# Revit family: Sink-Wall_Hung-American Standard-Comrade-0124.024
name_source: partatom
category: Plumbing Fixtures
units: mm (PartAtom-declared; Revit-internal decimal feet)

## family parameters
Cut with Voids When Loaded = No
Host = Face
OmniClass Number = 23.45.05.14.14
OmniClass Title = Sinks/Lavatories
Part Type = Normal
Room Calculation Point = No
Round Connector Dimension = Use Diameter
Shared = Yes

## types (1)
- 0124024.020
    ASME A112.19.2M for Vitreous China Fixtures = Yes
    Assembly Code = D2010310
    Bowl Depth = 6 1/4"
    CW Connection = Yes
    CWFU = 1.5
    Cold Water Connection Diameter = 1/2"
    Default Elevation = 30"
    Description = Comrade™ Wall-Hung Sink With 4-Inch Centerset, Wall Hanger Included
    Elevation Adjustment = 31"
    Finish = Vitreous China-American Standard-020-White
    HW Connection = Yes
    HWFU = 1.5
    Height = 9 1/2"
    Hot Water Connection Diameter = 1/2"
    Length = 18 1/4"
    Manufacturer = American Standard
    Material = Vitreous China-American Standard-020-White
    Model = 0124024.020
    Product Documentation Link = https://americanstandard.box.com
    Product URL = https://www.americanstandard-us.com
    Revised Date = 09/09/2021
    URL = http://www.americanstandard-us.com
    Vent Connection = No
    WFU = 2
    Waste Connection = Yes
    Waste Connection Diameter = 1 1/4"
    Width = 20"

## geometry (parser evidence)
native form markers: Sweep x2
no freeform markers — native parametric forms only
